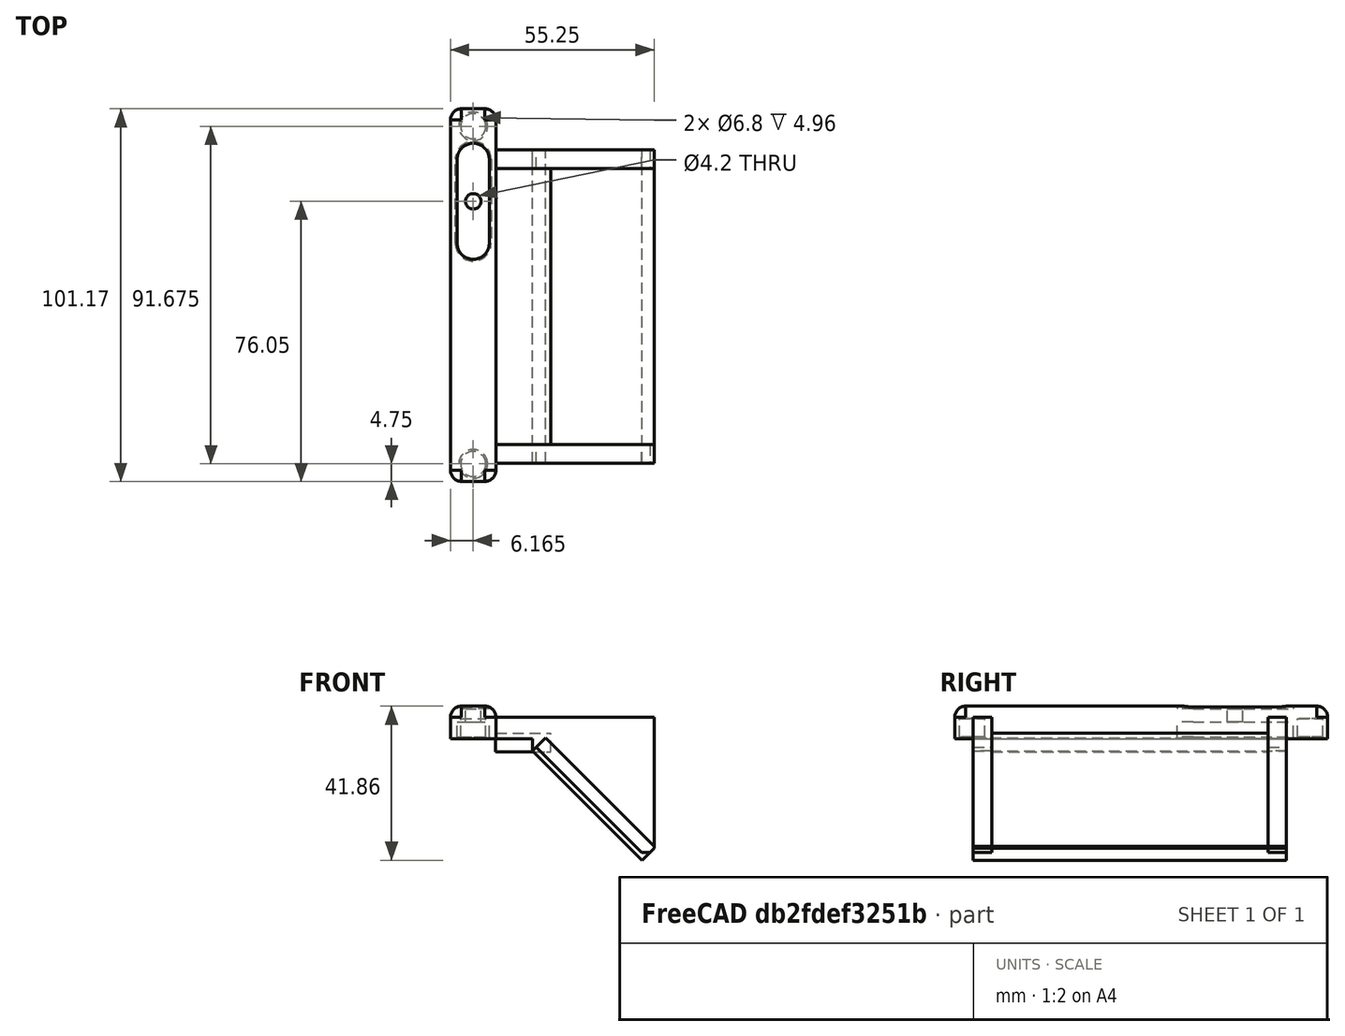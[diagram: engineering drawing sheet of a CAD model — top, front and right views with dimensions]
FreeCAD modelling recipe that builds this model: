
FCSTD DOCUMENT  (FreeCAD 1.0R39109 (Git))
Label: launch-stand-v2
License: All rights reserved
LicenseURL: https://en.wikipedia.org/wiki/All_rights_reserved
objects: Part::Box×13, Part::Cut×7, Part::MultiFuse×2, Part::Feature×1
note: 23 computed .brp shape members not serialized (recipe doc carries the construction recipe); baked Part::Feature solids carry a one-line shape summary decoded from their .brp

FEATURE [Part::Feature] Part__Feature  label="PN-000336 v7"
  shape: bbox 12.33 x 101.2 x 8.862 mm, 40 faces (baked)
FEATURE [Part::Box] Box  label="Cube"
  AttacherType = Attacher::AttachEngine3D
  Height = 5.85
  Length = 50
  Placement = pos=(12.25,5,0) rot=(0,0,1;0rad)
  Width = 5
FEATURE [Part::Box] Box001  label="Cube001"
  AttacherType = Attacher::AttachEngine3D
  Height = 5.85
  Length = 50
  Placement = pos=(12.25,85,0) rot=(0,0,1;0rad)
  Width = 5
FEATURE [Part::Box] Box002  label="Cube002"
  AttacherType = Attacher::AttachEngine3D
  Height = 30.85
  Length = 40
  Placement = pos=(22.25,5,-30.85) rot=(0,0,1;0rad)
  Width = 5
FEATURE [Part::Box] Box003  label="Cube003"
  AttacherType = Attacher::AttachEngine3D
  Height = 30.85
  Length = 40
  Placement = pos=(22.25,85,-30.85) rot=(0,0,1;0rad)
  Width = 5
FEATURE [Part::Box] Box004  label="Cube004"
  AttacherType = Attacher::AttachEngine3D
  Height = 42
  Length = 24
  Placement = pos=(36,5,-49) rot=(0,0.1,0;-0.785398rad)
  Width = 85
FEATURE [Part::Box] Box005  label="Cube005"
  AttacherType = Attacher::AttachEngine3D
  Height = 42
  Length = 24
  Placement = pos=(36,5,-49) rot=(0,0.1,0;-0.785398rad)
  Width = 85
FEATURE [Part::Cut] Cut
  Base = -> Box002
  Tool = -> Box004
FEATURE [Part::Box] Box006  label="Cube006"
  AttacherType = Attacher::AttachEngine3D
  Height = 42
  Length = 5
  Placement = pos=(52,5,-33) rot=(0,0.1,0;-0.785398rad)
  Width = 85
FEATURE [Part::Cut] Cut001
  Base = -> Box003
  Tool = -> Box005
FEATURE [Part::Box] Box007  label="Cube007"
  AttacherType = Attacher::AttachEngine3D
  Height = 36.85
  Length = 7
  Placement = pos=(55.25,5,-31) rot=(0,0,1;0rad)
  Width = 5
FEATURE [Part::MultiFuse] Fusion
  Shapes = -> [Cut,Box]
FEATURE [Part::Box] Box008  label="Cube008"
  AttacherType = Attacher::AttachEngine3D
  Height = 36.85
  Length = 7
  Placement = pos=(55.25,85,-31) rot=(0,0,1;0rad)
  Width = 5
FEATURE [Part::Cut] Cut002
  Base = -> Fusion
  Tool = -> Box007
FEATURE [Part::MultiFuse] Fusion001
  Shapes = -> [Box001,Cut001]
FEATURE [Part::Cut] Cut003
  Base = -> Fusion001
  Tool = -> Box008
FEATURE [Part::Box] Box009  label="Cube009"
  AttacherType = Attacher::AttachEngine3D
  Height = 42
  Length = 5
  Placement = pos=(82.4,5,-62) rot=(0,0.1,0;-0.785398rad)
  Width = 85
FEATURE [Part::Box] Box010  label="Cube010"
  AttacherType = Attacher::AttachEngine3D
  Height = 42
  Length = 5
  Placement = pos=(82.4,5,-62) rot=(0,0.1,0;-0.785398rad)
  Width = 85
FEATURE [Part::Cut] Cut004
  Base = -> Cut003
  Tool = -> Box009
FEATURE [Part::Cut] Cut005
  Base = -> Cut002
  Tool = -> Box010
FEATURE [Part::Box] Box011  label="Cube011"
  AttacherType = Attacher::AttachEngine3D
  Height = 10
  Length = 10
  Placement = pos=(55.25,5,-33) rot=(0,0,1;0rad)
  Width = 86
FEATURE [Part::Box] Box012  label="Cube012"
  AttacherType = Attacher::AttachEngine3D
  Height = 5
  Length = 15
  Placement = pos=(12.25,10,-3.5) rot=(0,0,1;0rad)
  Width = 75
FEATURE [Part::Cut] Cut006
  Base = -> Box006
  Tool = -> Box011
